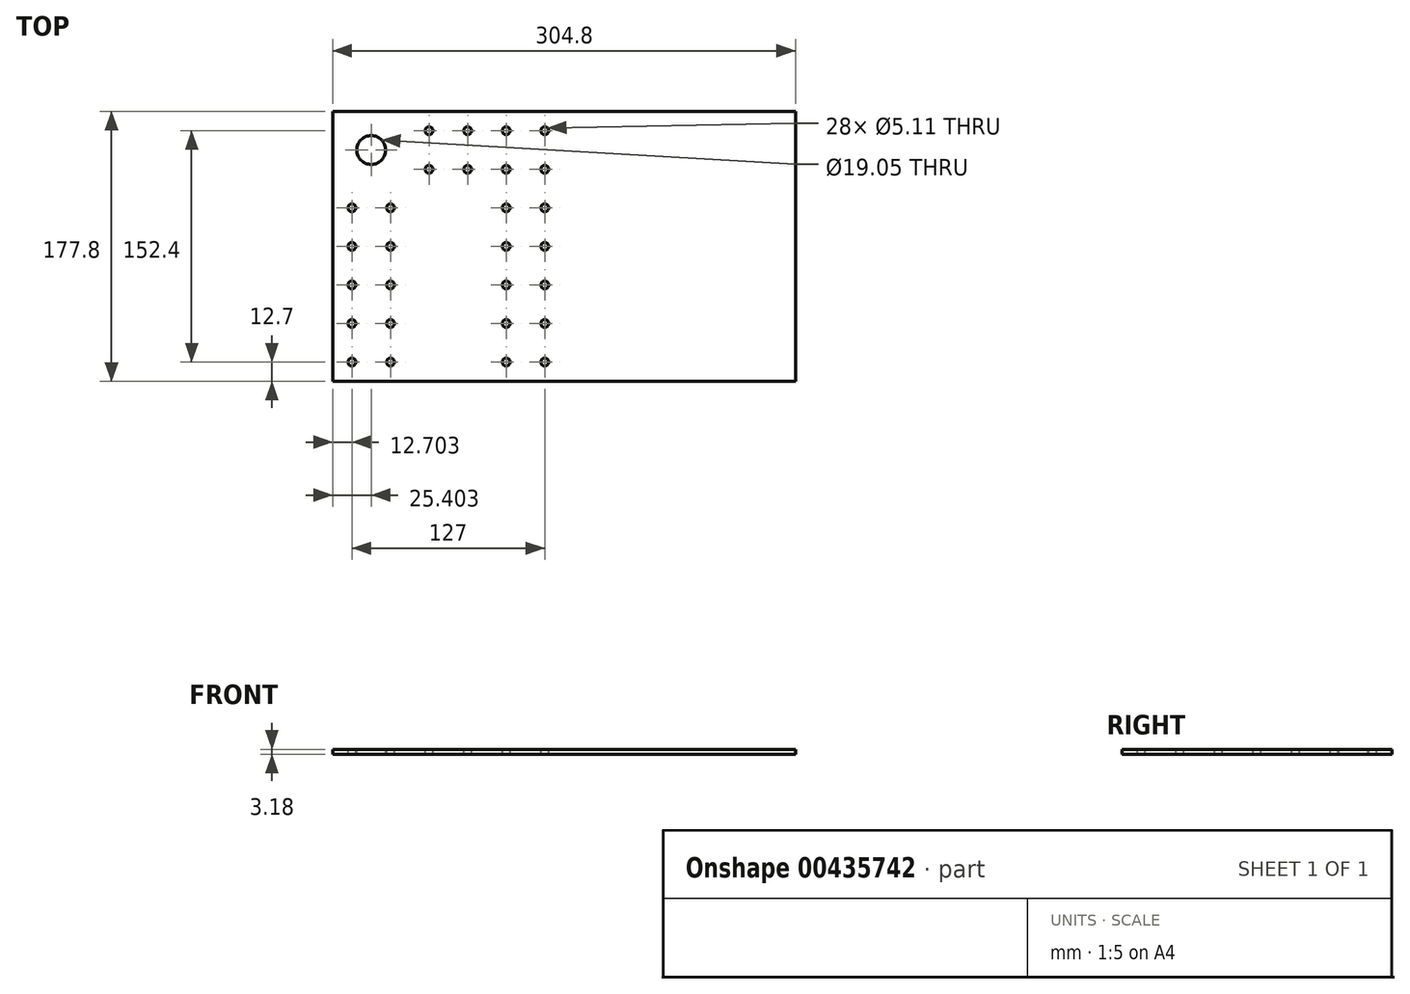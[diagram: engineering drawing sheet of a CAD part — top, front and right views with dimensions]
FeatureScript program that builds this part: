
annotation { "Feature Type Name" : "Feature", "Feature Type Description" : "" }
export const myFeature = defineFeature(function(context is Context, id is Id, definition is map)
    precondition{}
    {
        {
            var Q0;
            Q0=qCreatedBy(makeId("Top.planeOp"),FACE);
            var sketch = newSketch(context, id + "F0", { "sketchPlane" : qUnion([Q0])});
            skLineSegment(sketch, "E0.bottom", {"start": v(-147.98, 107.3) * mm, "end": v(156.82, 107.3) * mm});
            skLineSegment(sketch, "E0.top", {"start": v(-147.98, -70.5) * mm, "end": v(156.82, -70.5) * mm});
            skLineSegment(sketch, "E0.left", {"start": v(-147.98, 107.3) * mm, "end": v(-147.98, -70.5) * mm});
            skLineSegment(sketch, "E0.right", {"start": v(156.82, 107.3) * mm, "end": v(156.82, -70.5) * mm});
            skSolve(sketch);
        }
        {
            var Q0;
            Q0 = qSketchRegion(id + "F0", true);
            extrude(context, id + "F1", {"entities" : qUnion([Q0]), "depth" : 3.17 * mm});
        }
        {
            var Q0;
            Q0=makeQuery(id+"F1.opExtrude","CAP_FACE",FACE,{"disambiguationData":[OSD([sQuery(id+"F0.wireOp",EDGE,"E0.bottom"),sQuery(id+"F0.wireOp",EDGE,"E0.top"),sQuery(id+"F0.wireOp",EDGE,"E0.left"),sQuery(id+"F0.wireOp",EDGE,"E0.right")])],"isStart":false});
            var sketch = newSketch(context, id + "F2", { "sketchPlane" : qUnion([Q0])});
            skCircle(sketch, "E1", {"center": v(-135.28, -57.8) * mm, "radius": 2.55 * mm});
            skCircle(sketch, "E2.0.1.0", {"center": v(-135.28, -32.4) * mm, "radius": 2.55 * mm});
            skCircle(sketch, "E2.0.2.0", {"center": v(-135.28, -7) * mm, "radius": 2.55 * mm});
            skCircle(sketch, "E2.0.3.0", {"center": v(-135.28, 18.4) * mm, "radius": 2.55 * mm});
            skCircle(sketch, "E2.0.4.0", {"center": v(-135.28, 43.8) * mm, "radius": 2.55 * mm});
            skCircle(sketch, "E2.1.0.0", {"center": v(-109.88, -57.8) * mm, "radius": 2.55 * mm});
            skCircle(sketch, "E2.1.1.0", {"center": v(-109.88, -32.4) * mm, "radius": 2.55 * mm});
            skCircle(sketch, "E2.1.2.0", {"center": v(-109.88, -7) * mm, "radius": 2.55 * mm});
            skCircle(sketch, "E2.1.3.0", {"center": v(-109.88, 18.4) * mm, "radius": 2.55 * mm});
            skCircle(sketch, "E2.1.4.0", {"center": v(-109.88, 43.8) * mm, "radius": 2.55 * mm});
            skLineSegment(sketch, "E2.direction1", {"start": v(-135.28, -57.8) * mm, "end": v(-109.88, -57.8) * mm, "construction": true});
            skLineSegment(sketch, "E2.direction2", {"start": v(-135.28, -57.8) * mm, "end": v(-135.28, -32.4) * mm, "construction": true});
            skCircle(sketch, "E3", {"center": v(-122.58, 81.9) * mm, "radius": 10.86 * mm});
            skCircle(sketch, "E4", {"center": v(-84.48, 69.2) * mm, "radius": 2.55 * mm});
            skCircle(sketch, "E5.1.0.0", {"center": v(-59.08, 69.2) * mm, "radius": 2.55 * mm});
            skCircle(sketch, "E5.2.0.0", {"center": v(-33.68, 69.2) * mm, "radius": 2.55 * mm});
            skCircle(sketch, "E5.3.0.0", {"center": v(-8.28, 69.2) * mm, "radius": 2.55 * mm});
            skLineSegment(sketch, "E5.direction1", {"start": v(-84.48, 69.2) * mm, "end": v(-59.08, 69.2) * mm, "construction": true});
            skLineSegment(sketch, "E5.direction2", {"start": v(-84.48, 69.2) * mm, "end": v(-84.48, 43.8) * mm, "construction": true});
            skLineSegment(sketch, "E6", {"start": v(-109.88, 43.8) * mm, "end": v(-92.57, 43.8) * mm, "construction": true});
            skCircle(sketch, "E7.0.1.0", {"center": v(-84.48, 94.6) * mm, "radius": 2.55 * mm});
            skCircle(sketch, "E7.1.1.0", {"center": v(-59.08, 94.6) * mm, "radius": 2.55 * mm});
            skCircle(sketch, "E7.2.1.0", {"center": v(-33.68, 94.6) * mm, "radius": 2.55 * mm});
            skCircle(sketch, "E7.3.1.0", {"center": v(-8.28, 94.6) * mm, "radius": 2.55 * mm});
            skLineSegment(sketch, "E7.direction2", {"start": v(-84.48, 69.2) * mm, "end": v(-84.48, 94.6) * mm, "construction": true});
            skCircle(sketch, "E8.0.1.0", {"center": v(-33.68, 43.8) * mm, "radius": 2.55 * mm});
            skCircle(sketch, "E8.0.2.0", {"center": v(-33.68, 18.4) * mm, "radius": 2.55 * mm});
            skCircle(sketch, "E8.0.3.0", {"center": v(-33.68, -7) * mm, "radius": 2.55 * mm});
            skCircle(sketch, "E8.0.4.0", {"center": v(-33.68, -32.4) * mm, "radius": 2.55 * mm});
            skCircle(sketch, "E8.0.5.0", {"center": v(-33.68, -57.8) * mm, "radius": 2.55 * mm});
            skCircle(sketch, "E8.1.1.0", {"center": v(-8.28, 43.8) * mm, "radius": 2.55 * mm});
            skCircle(sketch, "E8.1.2.0", {"center": v(-8.28, 18.4) * mm, "radius": 2.55 * mm});
            skCircle(sketch, "E8.1.3.0", {"center": v(-8.28, -7) * mm, "radius": 2.55 * mm});
            skCircle(sketch, "E8.1.4.0", {"center": v(-8.28, -32.4) * mm, "radius": 2.55 * mm});
            skCircle(sketch, "E8.1.5.0", {"center": v(-8.28, -57.8) * mm, "radius": 2.55 * mm});
            skLineSegment(sketch, "E8.direction1", {"start": v(-33.68, 69.2) * mm, "end": v(-8.28, 69.2) * mm, "construction": true});
            skLineSegment(sketch, "E8.direction2", {"start": v(-33.68, 69.2) * mm, "end": v(-33.68, 43.8) * mm, "construction": true});
            skSolve(sketch);
        }
        {
            var Q0;
            Q0=sQuery(id+"F2.wireOp",VERTEX,"E8.0.4.0.center");
            var Q1;
            Q1=sQuery(id+"F2.wireOp",VERTEX,"E7.2.1.0.center");
            var Q2;
            Q2=sQuery(id+"F2.wireOp",VERTEX,"E8.0.1.0.center");
            var Q3;
            Q3=sQuery(id+"F2.wireOp",VERTEX,"E8.1.1.0.center");
            var Q4;
            Q4=sQuery(id+"F2.wireOp",VERTEX,"E8.0.5.0.center");
            var Q5;
            Q5=sQuery(id+"F2.wireOp",VERTEX,"E8.1.2.0.center");
            var Q6;
            Q6=sQuery(id+"F2.wireOp",VERTEX,"E8.1.3.0.center");
            var Q7;
            Q7=sQuery(id+"F2.wireOp",VERTEX,"E8.1.5.0.center");
            var Q8;
            Q8=sQuery(id+"F2.wireOp",VERTEX,"E7.direction2.end");
            var Q9;
            Q9=sQuery(id+"F2.wireOp",VERTEX,"E7.3.1.0.center");
            var Q10;
            Q10=sQuery(id+"F2.wireOp",VERTEX,"E8.1.4.0.center");
            var Q11;
            Q11=sQuery(id+"F2.wireOp",VERTEX,"E5.direction1.end");
            var Q12;
            Q12=sQuery(id+"F2.wireOp",VERTEX,"E8.0.2.0.center");
            var Q13;
            Q13=sQuery(id+"F2.wireOp",VERTEX,"E7.1.1.0.center");
            var Q14;
            Q14=sQuery(id+"F2.wireOp",VERTEX,"E8.0.3.0.center");
            var Q15;
            Q15=sQuery(id+"F2.wireOp",VERTEX,"E5.3.0.0.center");
            var Q16;
            Q16=sQuery(id+"F2.wireOp",VERTEX,"E4.center");
            var Q17;
            Q17=sQuery(id+"F2.wireOp",VERTEX,"E8.direction2.start");
            var Q18;
            Q18=sQuery(id+"F2.wireOp",VERTEX,"E2.0.4.0.center");
            var Q19;
            Q19=sQuery(id+"F2.wireOp",VERTEX,"E2.0.3.0.center");
            var Q20;
            Q20=sQuery(id+"F2.wireOp",VERTEX,"E2.1.1.0.center");
            var Q21;
            Q21=sQuery(id+"F2.wireOp",VERTEX,"E6.start");
            var Q22;
            Q22=sQuery(id+"F2.wireOp",VERTEX,"E2.direction1.end");
            var Q23;
            Q23=sQuery(id+"F2.wireOp",VERTEX,"E2.direction1.start");
            var Q24;
            Q24=sQuery(id+"F2.wireOp",VERTEX,"E2.1.2.0.center");
            var Q25;
            Q25=sQuery(id+"F2.wireOp",VERTEX,"E2.0.1.0.center");
            var Q26;
            Q26=sQuery(id+"F2.wireOp",VERTEX,"E2.1.3.0.center");
            var Q27;
            Q27=sQuery(id+"F2.wireOp",VERTEX,"E2.0.2.0.center");
            var Q28;
            Q28=makeQuery(id+"F1.opExtrude","SWEPT_BODY",BODY,{"disambiguationData":[OSD([sQuery(id+"F0.wireOp",EDGE,"E0.bottom"),sQuery(id+"F0.wireOp",EDGE,"E0.top"),sQuery(id+"F0.wireOp",EDGE,"E0.left"),sQuery(id+"F0.wireOp",EDGE,"E0.right")])]});
            hole(context, id + "F3", {"style" : HoleStyle.SIMPLE, "endStyle" : HoleEndStyle.THROUGH, "holeDiameter" : 5.1 * mm, "isTappedThrough" : true, "tappedDepth" : 12.7 * mm, "tapClearance" : 3, "locations" : qUnion([Q0, Q1, Q2, Q3, Q4, Q5, Q6, Q7, Q8, Q9, Q10, Q11, Q12, Q13, Q14, Q15, Q16, Q17, Q18, Q19, Q20, Q21, Q22, Q23, Q24, Q25, Q26, Q27]), "scope" : qUnion([Q28])});
        }
        {
            var Q0;
            Q0=sQuery(id+"F2.wireOp",VERTEX,"E3.center");
            var Q1;
            Q1=makeQuery(id+"F1.opExtrude","SWEPT_BODY",BODY,{"disambiguationData":[OSD([sQuery(id+"F0.wireOp",EDGE,"E0.bottom"),sQuery(id+"F0.wireOp",EDGE,"E0.top"),sQuery(id+"F0.wireOp",EDGE,"E0.left"),sQuery(id+"F0.wireOp",EDGE,"E0.right")])]});
            hole(context, id + "F4", {"style" : HoleStyle.SIMPLE, "endStyle" : HoleEndStyle.THROUGH, "holeDiameter" : 19.05 * mm, "isTappedThrough" : true, "tappedDepth" : 12.7 * mm, "tapClearance" : 3, "locations" : qUnion([Q0]), "scope" : qUnion([Q1])});
        }
    });
